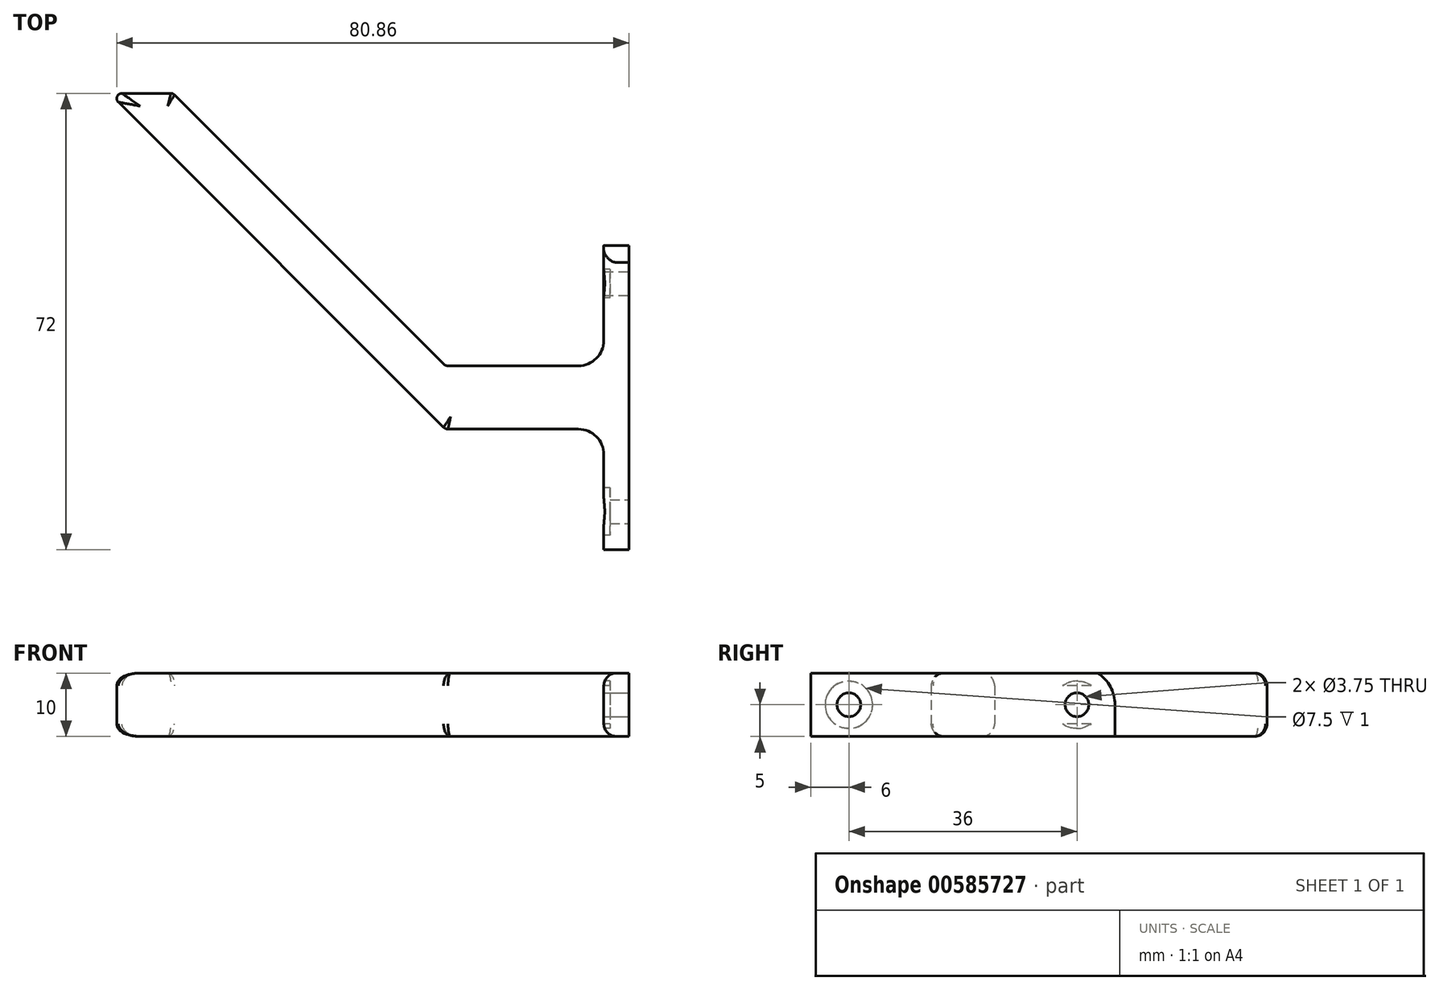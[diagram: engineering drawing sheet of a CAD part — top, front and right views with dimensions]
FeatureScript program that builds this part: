
annotation { "Feature Type Name" : "Feature", "Feature Type Description" : "" }
export const myFeature = defineFeature(function(context is Context, id is Id, definition is map)
    precondition{}
    {
        {
            var Q0;
            Q0=qCreatedBy(makeId("Top.planeOp"),FACE);
            var sketch = newSketch(context, id + "F0", { "sketchPlane" : qUnion([Q0])});
            skLineSegment(sketch, "E0.bottom", {"start": v(-12.09, -5) * mm, "end": v(12.5, -5) * mm});
            skLineSegment(sketch, "E0.top", {"start": v(-12.17, 5) * mm, "end": v(12.5, 5) * mm});
            skLineSegment(sketch, "E0.left", {"start": v(-12.5, -5) * mm, "end": v(-12.5, 5) * mm});
            skLineSegment(sketch, "E0.right", {"start": v(12.5, -5) * mm, "end": v(12.5, 5) * mm});
            skPoint(sketch, "E0.middle", {"position": v(0, 0) * mm});
            skLineSegment(sketch, "E1.bottom", {"start": v(12.5, 24) * mm, "end": v(16.5, 24) * mm});
            skLineSegment(sketch, "E1.top", {"start": v(12.5, -24) * mm, "end": v(16.5, -24) * mm});
            skLineSegment(sketch, "E1.left", {"start": v(12.5, 24) * mm, "end": v(12.5, -24) * mm});
            skLineSegment(sketch, "E1.right", {"start": v(16.5, 24) * mm, "end": v(16.5, -24) * mm});
            skLineSegment(sketch, "E2", {"start": v(-12.74, 5.24) * mm, "end": v(-55.26, 47.76) * mm});
            skLineSegment(sketch, "E3", {"start": v(-12.8, -4.7) * mm, "end": v(-64.12, 46.62) * mm});
            skLineSegment(sketch, "E4", {"start": v(-55.83, 48) * mm, "end": v(-63.55, 48) * mm});
            skPoint(sketch, "E5.visualSharp", {"position": v(-65.5, 48) * mm});
            skArc(sketch, "E5.filletArc", {"start": v(-63.55, 48) * mm, "mid": v(-64.3, 47.5) * mm, "end": v(-64.12, 46.62) * mm});
            skPoint(sketch, "E6.visualSharp", {"position": v(-55.5, 48) * mm});
            skArc(sketch, "E6.filletArc", {"start": v(-55.26, 47.76) * mm, "mid": v(-55.53, 47.94) * mm, "end": v(-55.83, 48) * mm});
            skPoint(sketch, "E7.visualSharp", {"position": v(-12.5, 5) * mm});
            skArc(sketch, "E7.filletArc", {"start": v(-12.74, 5.24) * mm, "mid": v(-12.47, 5.06) * mm, "end": v(-12.17, 5) * mm});
            skPoint(sketch, "E8.visualSharp", {"position": v(-12.5, -5) * mm});
            skArc(sketch, "E8.filletArc", {"start": v(-12.8, -4.7) * mm, "mid": v(-12.47, -4.92) * mm, "end": v(-12.09, -5) * mm});
            skArc(sketch, "E9", {"start": v(12.5, -9) * mm, "mid": v(11.33, -6.17) * mm, "end": v(8.5, -5) * mm});
            skArc(sketch, "E10", {"start": v(8.5, 5) * mm, "mid": v(11.33, 6.17) * mm, "end": v(12.5, 9) * mm});
            skSolve(sketch);
        }
        {
            var Q0;
            Q0 = qSketchRegion(id + "F0", true);
            extrude(context, id + "F1", {"entities" : qUnion([Q0]), "endBound" : BoundingType.SYMMETRIC, "depth" : 10 * mm, "offsetDistance" : 25 * mm});
        }
        {
            var Q0;
            Q0=makeQuery(id+"F1.opExtrude","SWEPT_FACE",FACE,{"disambiguationData":[OSD([sQuery(id+"F0.wireOp",EDGE,"E1.right")])]});
            var sketch = newSketch(context, id + "F2", { "sketchPlane" : qUnion([Q0])});
            skCircle(sketch, "E11", {"center": v(-18, 0) * mm, "radius": 1.88 * mm});
            skCircle(sketch, "E12", {"center": v(18, 0) * mm, "radius": 1.88 * mm});
            skCircle(sketch, "E13", {"center": v(-18, 0) * mm, "radius": 6 * mm});
            skCircle(sketch, "E14", {"center": v(18, 0) * mm, "radius": 6 * mm});
            skSolve(sketch);
        }
        {
            var Q0;
            Q0=makeQuery(id+"F2.imprint","IMPRINT",FACE,{"disambiguationData":[TD([[makeQuery(id+"F2.imprint","IMPRINT",EDGE,{"derivedFrom":sQuery(id+"F2.wireOp",EDGE,"E11")}),1.0]])]});
            var Q1;
            Q1=makeQuery(id+"F2.imprint","IMPRINT",FACE,{"disambiguationData":[TD([[makeQuery(id+"F2.imprint","IMPRINT",EDGE,{"derivedFrom":sQuery(id+"F2.wireOp",EDGE,"E12")}),1.0]])]});
            extrude(context, id + "F3", {"entities" : qUnion([Q0, Q1]), "operationType" : NewBodyOperationType.REMOVE, "endBound" : BoundingType.UP_TO_NEXT, "oppositeDirection" : true, "depth" : 25 * mm, "offsetDistance" : 25 * mm});
        }
        {
            var Q0;
            {var subQ0=sQuery(id+"F2.wireOp",EDGE,"E13");var subQ1=sQuery(id+"F0.wireOp",EDGE,"E1.right");var subQ2=makeQuery(id+"F1.opExtrude","CAP_EDGE",EDGE,{"disambiguationData":[OSD([subQ1])],"isStart":false});var subQ3=makeQuery(id+"F2.imprint","INTERSECT",VERTEX,{"disambiguationData":[OD(0.0)],"derivedFrom":[subQ2,subQ0]});Q0=makeQuery(id+"F2.imprint","IMPRINT",FACE,{"disambiguationData":[TD([[makeQuery(id+"F2.imprint","IMPRINT",EDGE,{"disambiguationData":[TD([[subQ3,-1.0]])],"derivedFrom":subQ0}),-1.0]])]});}
            var Q1;
            {var subQ0=sQuery(id+"F2.wireOp",EDGE,"E13");var subQ1=sQuery(id+"F0.wireOp",EDGE,"E1.right");var subQ4=makeQuery(id+"F1.opExtrude","CAP_EDGE",EDGE,{"disambiguationData":[OSD([subQ1])],"isStart":true});var subQ5=makeQuery(id+"F2.imprint","INTERSECT",VERTEX,{"disambiguationData":[OD(0.0)],"derivedFrom":[subQ4,subQ0]});Q1=makeQuery(id+"F2.imprint","IMPRINT",FACE,{"disambiguationData":[TD([[makeQuery(id+"F2.imprint","IMPRINT",EDGE,{"disambiguationData":[TD([[subQ5,1.0]])],"derivedFrom":subQ0}),-1.0]])]});}
            var Q2;
            {var subQ0=sQuery(id+"F2.wireOp",EDGE,"E14");var subQ1=sQuery(id+"F0.wireOp",EDGE,"E1.right");var subQ2=makeQuery(id+"F1.opExtrude","CAP_EDGE",EDGE,{"disambiguationData":[OSD([subQ1])],"isStart":false});var subQ3=makeQuery(id+"F2.imprint","INTERSECT",VERTEX,{"disambiguationData":[OD(0.0)],"derivedFrom":[subQ2,subQ0]});Q2=makeQuery(id+"F2.imprint","IMPRINT",FACE,{"disambiguationData":[TD([[makeQuery(id+"F2.imprint","IMPRINT",EDGE,{"disambiguationData":[TD([[subQ3,1.0]])],"derivedFrom":subQ0}),-1.0]])]});}
            var Q3;
            {var subQ0=sQuery(id+"F2.wireOp",EDGE,"E14");var subQ1=sQuery(id+"F0.wireOp",EDGE,"E1.right");var subQ4=makeQuery(id+"F1.opExtrude","CAP_EDGE",EDGE,{"disambiguationData":[OSD([subQ1])],"isStart":true});var subQ5=makeQuery(id+"F2.imprint","INTERSECT",VERTEX,{"disambiguationData":[OD(1.0)],"derivedFrom":[subQ4,subQ0]});Q3=makeQuery(id+"F2.imprint","IMPRINT",FACE,{"disambiguationData":[TD([[makeQuery(id+"F2.imprint","IMPRINT",EDGE,{"disambiguationData":[TD([[subQ5,-1.0]])],"derivedFrom":subQ0}),-1.0]])]});}
            extrude(context, id + "F4", {"entities" : qUnion([Q0, Q1, Q2, Q3]), "operationType" : NewBodyOperationType.REMOVE, "endBound" : BoundingType.UP_TO_NEXT, "oppositeDirection" : true, "depth" : 25 * mm, "offsetDistance" : 25 * mm});
        }
        {
            var Q0;
            Q0=makeQuery(id+"F1.opExtrude","CAP_EDGE",EDGE,{"disambiguationData":[OSD([sQuery(id+"F0.wireOp",EDGE,"E0.top")])],"isStart":false});
            var Q1;
            Q1=makeQuery(id+"F1.opExtrude","CAP_EDGE",EDGE,{"disambiguationData":[OSD([sQuery(id+"F0.wireOp",EDGE,"E0.top")])],"isStart":true});
            fillet(context, id + "F5", {"entities" : qUnion([Q0, Q1]), "radius" : 2 * mm, "tangentPropagation" : true, "allowEdgeOverflow" : false});
        }
        {
            var Q0;
            {var subQ0=sQuery(id+"F0.wireOp",EDGE,"E1.left");Q0=makeQuery(id+"F1.opExtrude","SWEPT_FACE",FACE,{"disambiguationData":[OSD([subQ0]),TDD([makeQuery(id+"F0.imprint","IMPRINT",EDGE,{"disambiguationData":[TD([[makeQuery(id+"F0.imprint","INTERSECT",VERTEX,{"derivedFrom":[sQuery(id+"F0.wireOp",EDGE,"E1.bottom"),subQ0]}),-1.0]])],"derivedFrom":subQ0})])]});}
            var sketch = newSketch(context, id + "F6", { "sketchPlane" : qUnion([Q0])});
            skCircle(sketch, "E15", {"center": v(-18, 0) * mm, "radius": 3.75 * mm});
            skCircle(sketch, "E16", {"center": v(18, 0) * mm, "radius": 3.75 * mm});
            skSolve(sketch);
        }
        {
            var Q0;
            Q0=makeQuery(id+"F6.imprint","IMPRINT",FACE,{"disambiguationData":[TD([[makeQuery(id+"F6.imprint","IMPRINT",EDGE,{"derivedFrom":makeQuery(id+"F3.boolean.opBoolean","COPY",EDGE,{"derivedFrom":makeQuery(id+"F3.opExtrude","CAP_EDGE",EDGE,{"disambiguationData":[OSD([sQuery(id+"F2.wireOp",EDGE,"E12")])],"isStart":false})})}),-1.0]])]});
            var Q1;
            {var subQ0=sQuery(id+"F6.wireOp",EDGE,"E15");var subQ1=sQuery(id+"F0.wireOp",EDGE,"E1.left");var subQ2=makeQuery(id+"F0.imprint","IMPRINT",EDGE,{"disambiguationData":[TD([[makeQuery(id+"F0.imprint","INTERSECT",VERTEX,{"derivedFrom":[sQuery(id+"F0.wireOp",EDGE,"E1.bottom"),subQ1]}),-1.0]])],"derivedFrom":subQ1});var subQ3=makeQuery(id+"F5.opFillet","BLEND_EDGE",EDGE,{"blendedFrom":[makeQuery(id+"F1.opExtrude","CAP_EDGE",EDGE,{"disambiguationData":[OSD([subQ1]),TDD([subQ2])],"isStart":false}),makeQuery(id+"F1.opExtrude","SWEPT_FACE",FACE,{"disambiguationData":[OSD([subQ1]),TDD([subQ2])]})],"blendedInto":[makeQuery(id+"F1.opExtrude","SWEPT_FACE",FACE,{"disambiguationData":[OSD([subQ1]),TDD([subQ2])]})]});var subQ4=makeQuery(id+"F6.imprint","INTERSECT",VERTEX,{"disambiguationData":[OD(0.0)],"derivedFrom":[subQ3,subQ0]});Q1=makeQuery(id+"F6.imprint","IMPRINT",FACE,{"disambiguationData":[TD([[makeQuery(id+"F6.imprint","IMPRINT",EDGE,{"disambiguationData":[TD([[subQ4,1.0]])],"derivedFrom":subQ0}),1.0]])]});}
            var Q2;
            {var subQ0=sQuery(id+"F6.wireOp",EDGE,"E15");var subQ1=sQuery(id+"F0.wireOp",EDGE,"E1.left");var subQ2=makeQuery(id+"F0.imprint","IMPRINT",EDGE,{"disambiguationData":[TD([[makeQuery(id+"F0.imprint","INTERSECT",VERTEX,{"derivedFrom":[sQuery(id+"F0.wireOp",EDGE,"E1.bottom"),subQ1]}),-1.0]])],"derivedFrom":subQ1});var subQ3=makeQuery(id+"F5.opFillet","BLEND_EDGE",EDGE,{"blendedFrom":[makeQuery(id+"F1.opExtrude","CAP_EDGE",EDGE,{"disambiguationData":[OSD([subQ1]),TDD([subQ2])],"isStart":true}),makeQuery(id+"F1.opExtrude","SWEPT_FACE",FACE,{"disambiguationData":[OSD([subQ1]),TDD([subQ2])]})],"blendedInto":[makeQuery(id+"F1.opExtrude","SWEPT_FACE",FACE,{"disambiguationData":[OSD([subQ1]),TDD([subQ2])]})]});var subQ4=makeQuery(id+"F6.imprint","INTERSECT",VERTEX,{"disambiguationData":[OD(0.0)],"derivedFrom":[subQ3,subQ0]});Q2=makeQuery(id+"F6.imprint","IMPRINT",FACE,{"disambiguationData":[TD([[makeQuery(id+"F6.imprint","IMPRINT",EDGE,{"disambiguationData":[TD([[subQ4,-1.0]])],"derivedFrom":subQ0}),1.0]])]});}
            var Q3;
            Q3=makeQuery(id+"F6.imprint","IMPRINT",FACE,{"disambiguationData":[TD([[makeQuery(id+"F6.imprint","IMPRINT",EDGE,{"derivedFrom":sQuery(id+"F6.wireOp",EDGE,"E16")}),1.0]])]});
            extrude(context, id + "F7", {"entities" : qUnion([Q0, Q1, Q2, Q3]), "operationType" : NewBodyOperationType.REMOVE, "oppositeDirection" : true, "depth" : 1 * mm, "offsetDistance" : 25 * mm});
        }
    });
